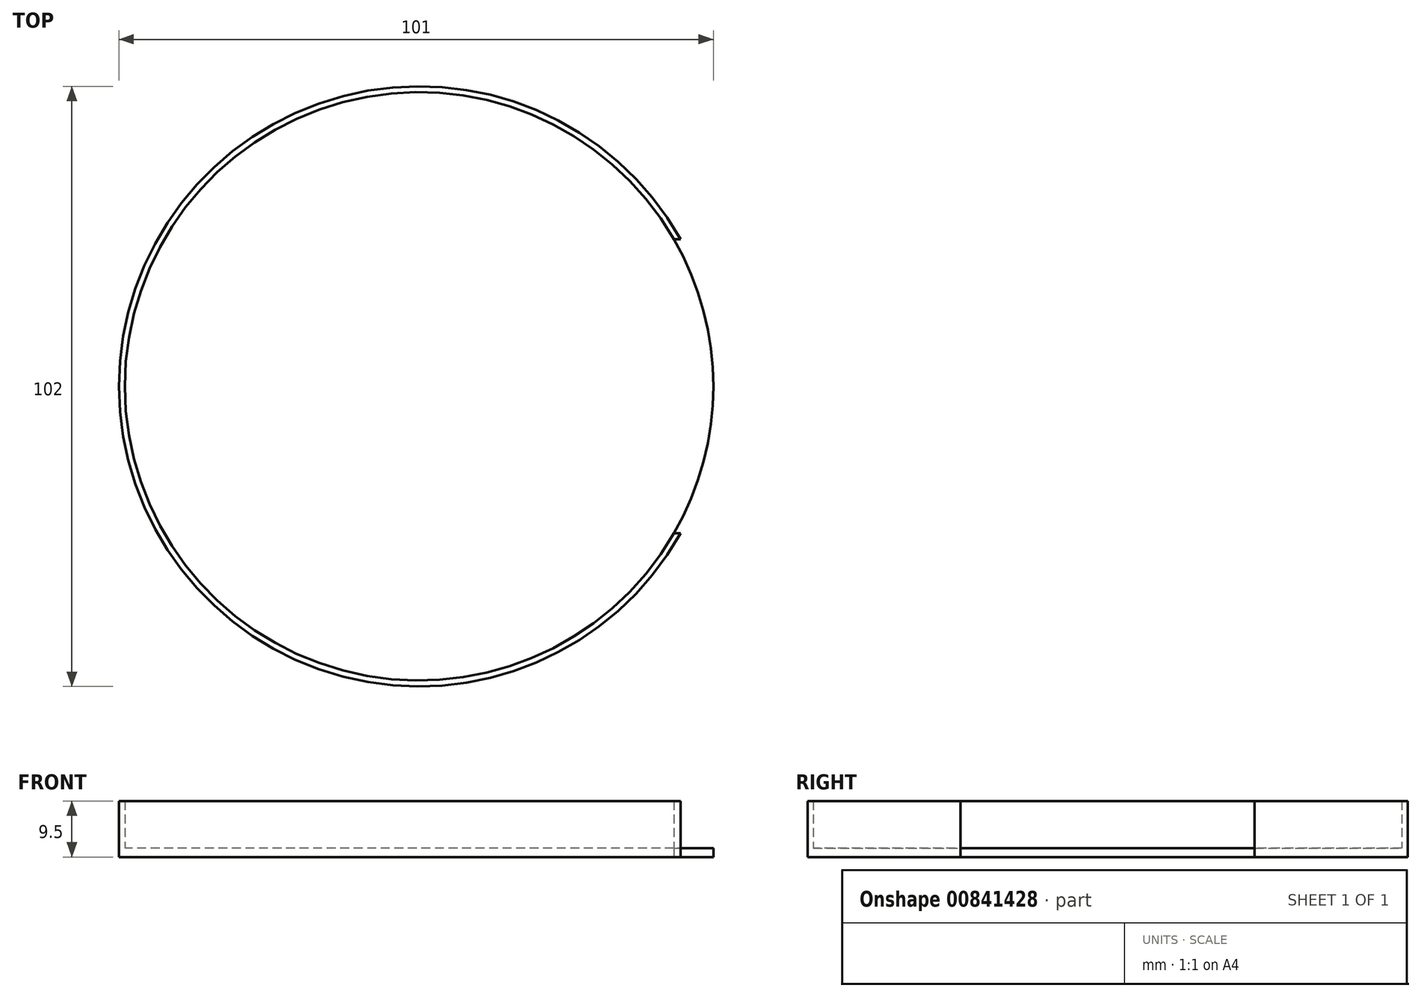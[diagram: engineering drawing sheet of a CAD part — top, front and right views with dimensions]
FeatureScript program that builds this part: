
annotation { "Feature Type Name" : "Feature", "Feature Type Description" : "" }
export const myFeature = defineFeature(function(context is Context, id is Id, definition is map)
    precondition{}
    {
        {
            var Q0;
            Q0=qCreatedBy(makeId("Top.planeOp"),FACE);
            var sketch = newSketch(context, id + "F0", { "sketchPlane" : qUnion([Q0])});
            skCircle(sketch, "E0", {"center": v(1.66, 0) * mm, "radius": 50 * mm});
            skSolve(sketch);
        }
        {
            var Q0;
            Q0 = qSketchRegion(id + "F0", true);
            extrude(context, id + "F1", {"entities" : qUnion([Q0]), "depth" : 1.5 * mm, "offsetDistance" : 25 * mm});
        }
        {
            var Q0;
            Q0=makeQuery(id+"F1.opExtrude","CAP_FACE",FACE,{"disambiguationData":[OSD([sQuery(id+"F0.wireOp",EDGE,"E0")])],"isStart":false});
            var sketch = newSketch(context, id + "F2", { "sketchPlane" : qUnion([Q0])});
            skArc(sketch, "E1.0", {"start": v(44.96, 25) * mm, "mid": v(-48.34, 0) * mm, "end": v(44.96, -25) * mm});
            skArc(sketch, "E2.0", {"start": v(46.11, 25) * mm, "mid": v(-49.34, 0) * mm, "end": v(46.11, -25) * mm});
            skLineSegment(sketch, "E3", {"start": v(46.11, -25) * mm, "end": v(44.96, -25) * mm});
            skLineSegment(sketch, "E4", {"start": v(46.11, 25) * mm, "end": v(44.96, 25) * mm});
            skLineSegment(sketch, "E5", {"start": v(46.11, -25) * mm, "end": v(46.11, 25) * mm, "construction": true});
            skSolve(sketch);
        }
        {
            var Q0;
            Q0 = qSketchRegion(id + "F2", true);
            var Q1;
            Q1=makeQuery(id+"F1.opExtrude","CAP_FACE",FACE,{"disambiguationData":[OSD([sQuery(id+"F0.wireOp",EDGE,"E0")])],"isStart":true});
            extrude(context, id + "F3", {"entities" : qUnion([Q0]), "operationType" : NewBodyOperationType.ADD, "depth" : 8 * mm, "offsetDistance" : 25 * mm, "hasSecondDirection" : true, "secondDirectionBound" : SecondDirectionBoundingType.UP_TO_SURFACE, "secondDirectionOppositeDirection" : true, "secondDirectionDepth" : 25 * mm, "secondDirectionBoundEntityFace" : qUnion([Q1])});
        }
    });
